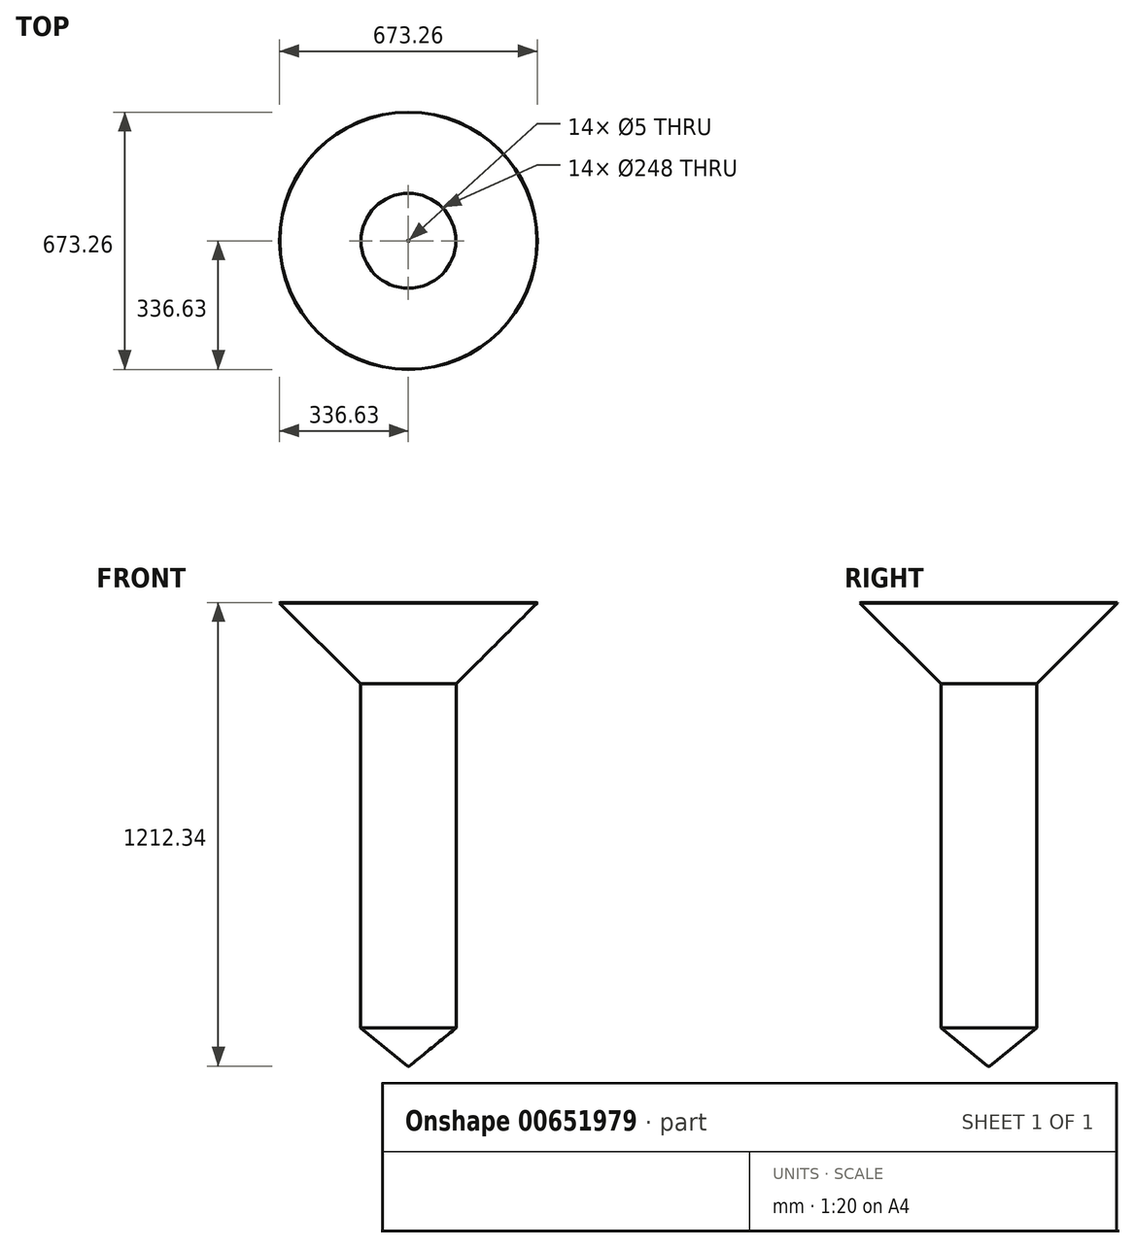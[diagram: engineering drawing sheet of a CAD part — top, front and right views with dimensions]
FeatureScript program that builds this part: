
annotation { "Feature Type Name" : "Feature", "Feature Type Description" : "" }
export const myFeature = defineFeature(function(context is Context, id is Id, definition is map)
    precondition{}
    {
        {
            var Q0;
            Q0=qCreatedBy(makeId("Front.planeOp"),FACE);
            var sketch = newSketch(context, id + "F0", { "sketchPlane" : qUnion([Q0])});
            skLineSegment(sketch, "E0", {"start": v(125, 496.75) * mm, "end": v(125, -403.25) * mm});
            skLineSegment(sketch, "E1", {"start": v(2.5, -503.25) * mm, "end": v(125, -403.25) * mm});
            skLineSegment(sketch, "E2", {"start": v(124, 496.75) * mm, "end": v(124, -403.25) * mm});
            skLineSegment(sketch, "E3", {"start": v(2.5, -502.25) * mm, "end": v(124, -403.25) * mm});
            skLineSegment(sketch, "E4", {"start": v(2.5, -503.25) * mm, "end": v(2.5, -502.25) * mm});
            skLineSegment(sketch, "E5.trimOffspring", {"start": v(124, -503.25) * mm, "end": v(125, -503.25) * mm});
            skLineSegment(sketch, "E6", {"start": v(125, 496.75) * mm, "end": v(336.63, 708.38) * mm});
            skLineSegment(sketch, "E7", {"start": v(124, 496.75) * mm, "end": v(335.92, 709.09) * mm});
            skLineSegment(sketch, "E8", {"start": v(0, 0) * mm, "end": v(0, -529.2) * mm, "construction": true});
            skLineSegment(sketch, "E9", {"start": v(336.63, 708.38) * mm, "end": v(335.92, 709.09) * mm});
            skSolve(sketch);
        }
        {
            var Q0;
            Q0=makeQuery(id+"F0.imprint","IMPRINT",FACE,{"disambiguationData":[TD([[makeQuery(id+"F0.imprint","IMPRINT",EDGE,{"derivedFrom":sQuery(id+"F0.wireOp",EDGE,"E0")}),-1.0]])]});
            var Q1;
            Q1=sQuery(id+"F0.wireOp",EDGE,"E8");
            revolve(context, id + "F1", {"entities" : qUnion([Q0]), "axis" : qUnion([Q1]), "revolveType" : RevolveType.FULL});
        }
    });
